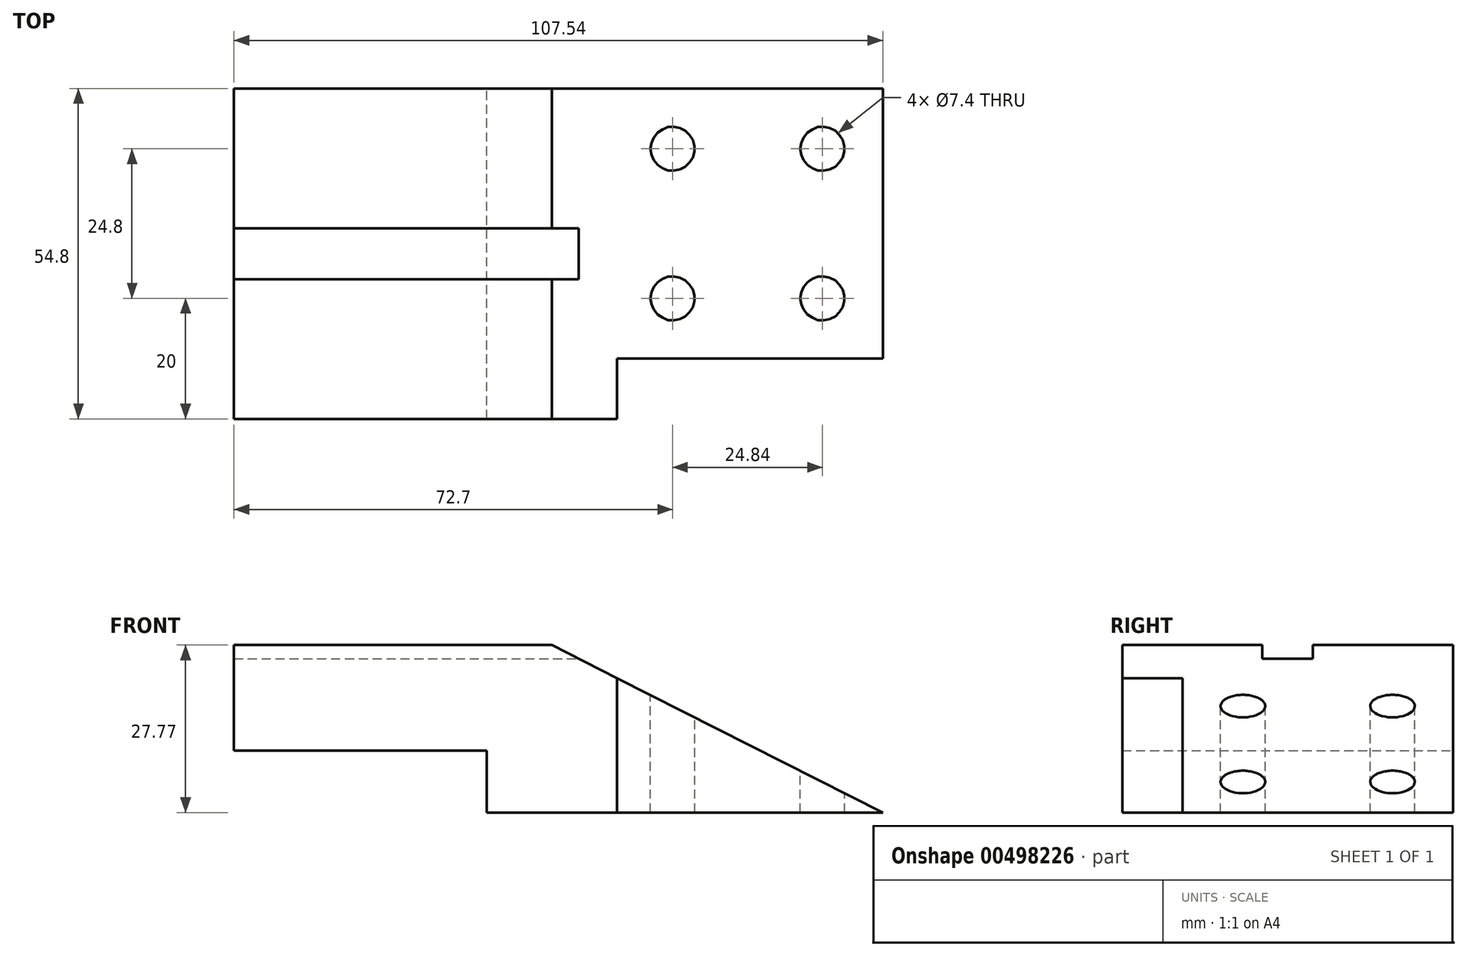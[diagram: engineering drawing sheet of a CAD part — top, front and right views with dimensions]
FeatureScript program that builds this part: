
annotation { "Feature Type Name" : "Feature", "Feature Type Description" : "" }
export const myFeature = defineFeature(function(context is Context, id is Id, definition is map)
    precondition{}
    {
        {
            var Q0;
            Q0=qCreatedBy(makeId("Front.planeOp"),FACE);
            var sketch = newSketch(context, id + "F0", { "sketchPlane" : qUnion([Q0])});
            skLineSegment(sketch, "E0.bottom", {"start": v(0, 0) * mm, "end": v(-10.82, 0) * mm});
            skLineSegment(sketch, "E0.top", {"start": v(0, 27.77) * mm, "end": v(-52.7, 27.77) * mm});
            skLineSegment(sketch, "E0.left", {"start": v(0, 0) * mm, "end": v(0, 27.77) * mm});
            skLineSegment(sketch, "E0.right", {"start": v(-52.7, 10.25) * mm, "end": v(-52.7, 27.77) * mm});
            skLineSegment(sketch, "E1.top", {"start": v(-10.82, 10.25) * mm, "end": v(-52.7, 10.25) * mm});
            skLineSegment(sketch, "E1.left", {"start": v(-10.82, 0) * mm, "end": v(-10.82, 10.25) * mm});
            skLineSegment(sketch, "E2", {"start": v(0, 0) * mm, "end": v(10.82, 0) * mm});
            skLineSegment(sketch, "E3", {"start": v(0, 27.77) * mm, "end": v(54.84, 0) * mm});
            skLineSegment(sketch, "E4", {"start": v(54.84, 0) * mm, "end": v(10.82, 0) * mm});
            skLineSegment(sketch, "E5", {"start": v(10.82, 0) * mm, "end": v(10.82, 22.3) * mm, "construction": true});
            skSolve(sketch);
        }
        {
            var Q0;
            Q0=makeQuery(id+"F0.imprint","IMPRINT",FACE,{"disambiguationData":[TD([[makeQuery(id+"F0.imprint","IMPRINT",EDGE,{"derivedFrom":sQuery(id+"F0.wireOp",EDGE,"E0.bottom")}),-1.0]])]});
            var Q1;
            Q1=makeQuery(id+"F0.imprint","IMPRINT",FACE,{"disambiguationData":[TD([[makeQuery(id+"F0.imprint","IMPRINT",EDGE,{"derivedFrom":sQuery(id+"F0.wireOp",EDGE,"E0.left")}),-1.0]])]});
            extrude(context, id + "F1", {"entities" : qUnion([Q0, Q1]), "endBound" : BoundingType.SYMMETRIC, "depth" : 54.8 * mm});
        }
        {
            var Q0;
            Q0=makeQuery(id+"F1.opExtrude","CAP_FACE",FACE,{"disambiguationData":[OSD([sQuery(id+"F0.wireOp",EDGE,"E0.bottom"),sQuery(id+"F0.wireOp",EDGE,"E0.top"),sQuery(id+"F0.wireOp",EDGE,"E0.right"),sQuery(id+"F0.wireOp",EDGE,"E1.top"),sQuery(id+"F0.wireOp",EDGE,"E1.left"),sQuery(id+"F0.wireOp",EDGE,"E2"),sQuery(id+"F0.wireOp",EDGE,"E3"),sQuery(id+"F0.wireOp",EDGE,"E4")])],"isStart":false});
            var sketch = newSketch(context, id + "F2", { "sketchPlane" : qUnion([Q0])});
            skLineSegment(sketch, "E6.0", {"start": v(10.82, 0) * mm, "end": v(10.82, 22.3) * mm});
            skLineSegment(sketch, "E7.0", {"start": v(10.82, 22.3) * mm, "end": v(54.84, 0) * mm});
            skLineSegment(sketch, "E8.0", {"start": v(54.84, 0) * mm, "end": v(10.82, 0) * mm});
            skPoint(sketch, "E9.orphan", {"position": v(0, 27.77) * mm});
            skSolve(sketch);
        }
        {
            var Q0;
            Q0 = qSketchRegion(id + "F2", true);
            extrude(context, id + "F3", {"entities" : qUnion([Q0]), "operationType" : NewBodyOperationType.REMOVE, "oppositeDirection" : true, "depth" : 10 * mm});
        }
        {
            var Q0;
            Q0=qCreatedBy(makeId("Right.planeOp"),FACE);
            var sketch = newSketch(context, id + "F4", { "sketchPlane" : qUnion([Q0])});
            skLineSegment(sketch, "E10", {"start": v(0, 25.52) * mm, "end": v(-4.21, 25.52) * mm});
            skLineSegment(sketch, "E11", {"start": v(-4.21, 25.52) * mm, "end": v(-4.21, 28.77) * mm});
            skLineSegment(sketch, "E12.MirrorCS", {"start": v(4.21, 25.52) * mm, "end": v(4.21, 28.77) * mm});
            skLineSegment(sketch, "E13.MirrorCS", {"start": v(0, 25.52) * mm, "end": v(4.21, 25.52) * mm});
            skLineSegment(sketch, "E14", {"start": v(-4.21, 28.77) * mm, "end": v(4.21, 28.77) * mm});
            skSolve(sketch);
        }
        {
            var Q0;
            Q0=makeQuery(id+"F4.imprint","IMPRINT",FACE,{"disambiguationData":[TD([[makeQuery(id+"F4.imprint","IMPRINT",EDGE,{"derivedFrom":sQuery(id+"F4.wireOp",EDGE,"E10")}),-1.0]])]});
            extrude(context, id + "F5", {"entities" : qUnion([Q0]), "operationType" : NewBodyOperationType.REMOVE, "endBound" : BoundingType.SYMMETRIC, "oppositeDirection" : true, "depth" : 176.4 * mm});
        }
        {
            var Q0;
            {var subQ0=sQuery(id+"F4.wireOp",EDGE,"E11");var subQ3=sQuery(id+"F0.wireOp",EDGE,"E0.top");Q0=makeQuery(id+"F5.boolean.opBoolean","SPLIT",FACE,{"disambiguationData":[TD([makeQuery(id+"F5.opExtrude","SWEPT_FACE",FACE,{"disambiguationData":[OSD([subQ0])]})])],"derivedFrom":makeQuery(id+"F1.opExtrude","SWEPT_FACE",FACE,{"disambiguationData":[OSD([subQ3])]})});}
            var sketch = newSketch(context, id + "F6", { "sketchPlane" : qUnion([Q0])});
            skCircle(sketch, "E15", {"center": v(20, -7.4) * mm, "radius": 3.7 * mm});
            skCircle(sketch, "E16.0.1.0", {"center": v(20, 17.4) * mm, "radius": 3.7 * mm});
            skCircle(sketch, "E16.1.0.0", {"center": v(44.84, -7.4) * mm, "radius": 3.7 * mm});
            skCircle(sketch, "E16.1.1.0", {"center": v(44.84, 17.4) * mm, "radius": 3.7 * mm});
            skLineSegment(sketch, "E16.direction1", {"start": v(20, -7.4) * mm, "end": v(44.84, -7.4) * mm, "construction": true});
            skLineSegment(sketch, "E16.direction2", {"start": v(20, -7.4) * mm, "end": v(20, 17.4) * mm, "construction": true});
            skSolve(sketch);
        }
        {
            var Q0;
            Q0=makeQuery(id+"F6.imprint","IMPRINT",FACE,{"disambiguationData":[TD([[makeQuery(id+"F6.imprint","IMPRINT",EDGE,{"derivedFrom":sQuery(id+"F6.wireOp",EDGE,"E16.0.1.0")}),1.0]])]});
            var Q1;
            Q1=makeQuery(id+"F6.imprint","IMPRINT",FACE,{"disambiguationData":[TD([[makeQuery(id+"F6.imprint","IMPRINT",EDGE,{"derivedFrom":sQuery(id+"F6.wireOp",EDGE,"E16.1.1.0")}),1.0]])]});
            var Q2;
            Q2=makeQuery(id+"F6.imprint","IMPRINT",FACE,{"disambiguationData":[TD([[makeQuery(id+"F6.imprint","IMPRINT",EDGE,{"derivedFrom":sQuery(id+"F6.wireOp",EDGE,"E16.1.0.0")}),1.0]])]});
            var Q3;
            Q3=makeQuery(id+"F6.imprint","IMPRINT",FACE,{"disambiguationData":[TD([[makeQuery(id+"F6.imprint","IMPRINT",EDGE,{"derivedFrom":sQuery(id+"F6.wireOp",EDGE,"E15")}),1.0]])]});
            extrude(context, id + "F7", {"entities" : qUnion([Q0, Q1, Q2, Q3]), "operationType" : NewBodyOperationType.REMOVE, "endBound" : BoundingType.THROUGH_ALL, "oppositeDirection" : true, "depth" : 25 * mm});
        }
    });
